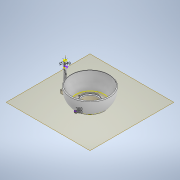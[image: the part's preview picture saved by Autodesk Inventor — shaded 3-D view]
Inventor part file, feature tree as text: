
AUTODESK INVENTOR PART (.ipt)
format: ipt  version: 2020 (Build 240168000, 168)  size: 521,216 bytes
history: native  units: in
note: dims shown in document units (in); Inventor stores cm internally (conversion verified against a paired STEP export)
features: sketch x9, extrude x4, hole x3, fillet x3, other x3, revolve x1, plane x1, mirror x1, helix x1
ambient origin geometry x8: Origin, YZ Plane, XZ Plane, XY Plane, X Axis, Y Axis, Z Axis, Center Point
bodies: Solid1 (feature_tree)
feature tree (26):
  revolve  "Revolution1"  [1 undecoded]
  plane  "Work Plane1"
  sketch  "Sketch2"  dims[d2=0.125in d3=3.0in]
  extrude  "Extrusion1"  Depth=3.0in
  hole  "Hole1"  [1 undecoded]
  hole  "Hole4"  [1 undecoded]
  hole  "Hole5"  [1 undecoded]
  fillet  "Fillet1"  Radius=0.85in
  mirror  "Mirror1"
  fillet  "Fillet2"  Radius=3.0in
  fillet  "Fillet3"  Radius=0.125in
  extrude  "Extrusion2"  TaperAngle=90.0deg  [1 undecoded]
  extrude  "Extrusion3"  Depth=0.3in
  extrude  "Extrusion4"  Depth=0.35in TaperAngle=0.0deg
  sketch  "3D Sketch1"
  other  "Work Axis1"
  helix  "Coil1"  [1 undecoded]
  sketch  "Sketch1"  dims[d0=1.26in d1=0.0in]
  other  "Work Point1"
  sketch  "Sketch4"  dims[d4=3.0in d5=1.0in]
  sketch  "Sketch5"  dims[d6=0.125in d7=1.0in]
  sketch  "Sketch6"  dims[d8=0.5in d9=0.125in d10=0.85in d11=3.0in d12=0.125in]
  sketch  "Sketch7"  dims[d13=3.0in d14=90.0deg]
  sketch  "Sketch8"  dims[d15=0.125in d16=0.75in d17=0.125in d18=0.25in d19=0.5635in d20=0.25in d21=0.0in d22=0.3in]
  other  "Helical Curve2"
  sketch  "Sketch9"  dims[d23=0.3in d24=0.35in d25=0.0in d41=1.75in d42=0.266in d43=0.75in d44=0.438in d45=0.25in d46=0.5635in d47=6.0in d48=0.0in d49=0.15in d50=0.125in d51=0.75in d52=0.438in d53=0.25in d54=0.5635in d55=0.2in d56=0.0in d57=0.0625in d58=0.125in d59=0.0625in d60=0.25in d61=90.0deg d62=0.5in d63=3.0in d64=0.25in d65=3.0in d66=0.25in d67=0.5in d68=0.5in d69=0.0in d70=0.375in d71=4.0in d72=0.0in d73=0.0625in d74=0.125in d75=0.025in d76=1.0in d77=0.0in d83=2.0in d84=0.0984in d85=0.549in d86=0.0in d87=0.125in d88=1.0in d89=1.0in d90=0.0984in d91=0.0in d92=90.0deg d93=90.0deg d94=45.0deg d95=0.0in]
note: 6 required parameter values undecoded (feature->parameter linkage not recoverable at this tier; creation-order binding heuristic only, values carry confidence <= 0.55)